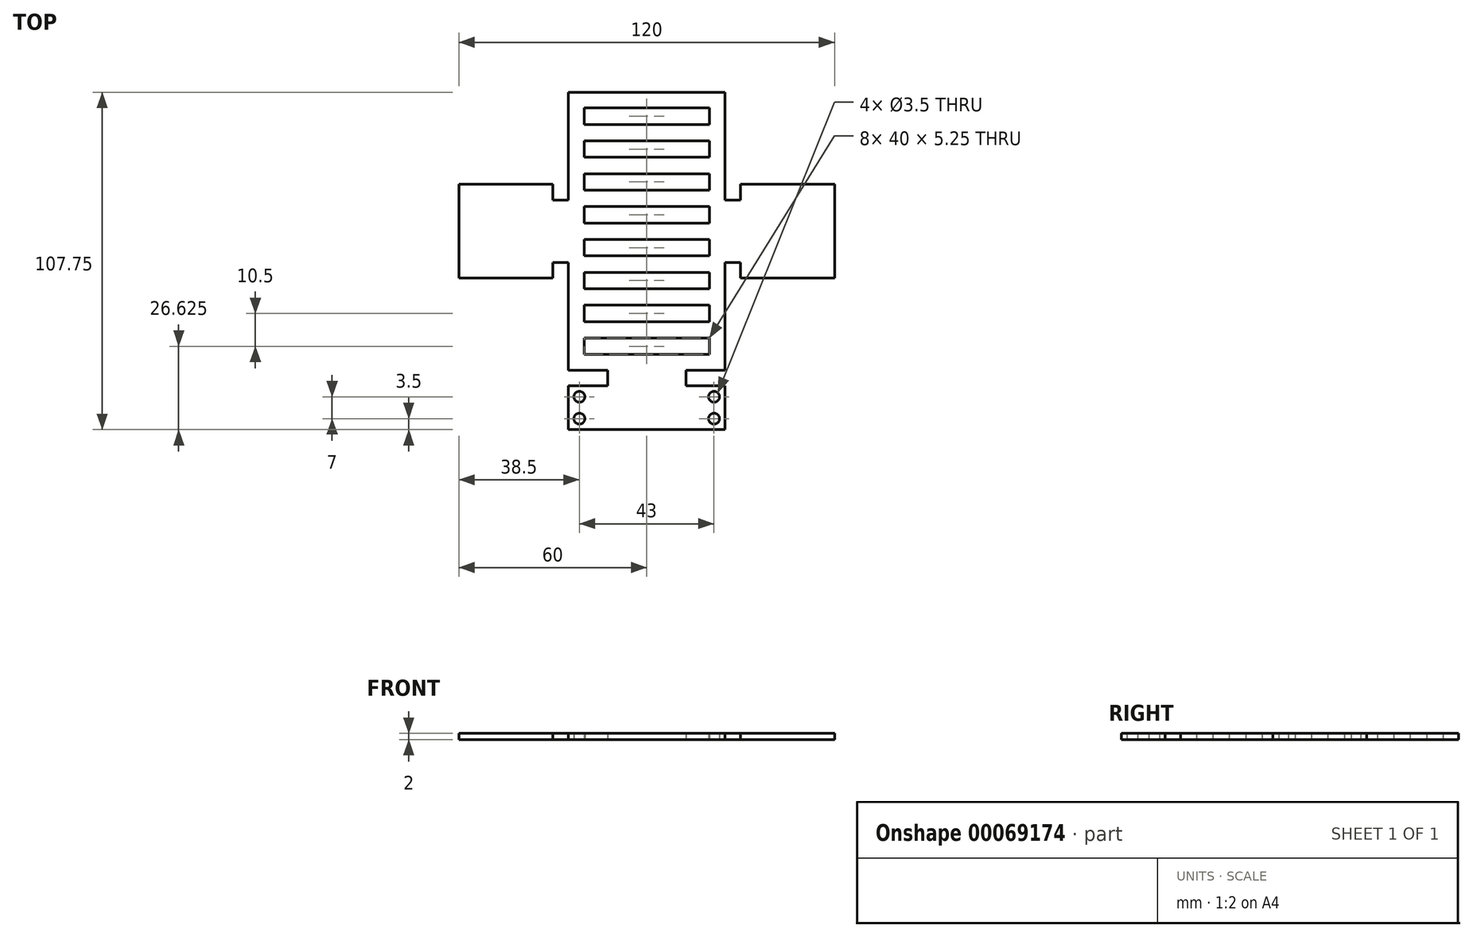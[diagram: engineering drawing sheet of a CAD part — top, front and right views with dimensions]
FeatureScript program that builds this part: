
annotation { "Feature Type Name" : "Feature", "Feature Type Description" : "" }
export const myFeature = defineFeature(function(context is Context, id is Id, definition is map)
    precondition{}
    {
        {
            var Q0;
            Q0=qCreatedBy(makeId("Top.planeOp"),FACE);
            var sketch = newSketch(context, id + "F0", { "sketchPlane" : qUnion([Q0])});
            skLineSegment(sketch, "E0", {"start": v(0, 0) * mm, "end": v(0, 29.37) * mm});
            skLineSegment(sketch, "E1", {"start": v(-5, 29.38) * mm, "end": v(-35, 29.38) * mm});
            skLineSegment(sketch, "E2", {"start": v(-35, 29.38) * mm, "end": v(-35, 59.38) * mm});
            skLineSegment(sketch, "E3", {"start": v(-35, 59.38) * mm, "end": v(-5, 59.38) * mm});
            skLineSegment(sketch, "E4", {"start": v(0, 59.38) * mm, "end": v(0, 88.75) * mm});
            skLineSegment(sketch, "E5", {"start": v(0, 88.75) * mm, "end": v(25, 88.75) * mm});
            skLineSegment(sketch, "E6", {"start": v(0, 0) * mm, "end": v(25, 0) * mm});
            skLineSegment(sketch, "E7", {"start": v(25, 88.75) * mm, "end": v(25, -19) * mm, "construction": true});
            skLineSegment(sketch, "E8", {"start": v(0, -5) * mm, "end": v(0, -19) * mm});
            skLineSegment(sketch, "E9", {"start": v(0, -19) * mm, "end": v(25, -19) * mm});
            skCircle(sketch, "E10.cCircle", {"center": v(-20, 44.37) * mm, "radius": 10 * mm, "construction": true});
            skPoint(sketch, "E10.cCircle.centerSnap0", {"position": v(-35, 44.38) * mm});
            skLineSegment(sketch, "E10.0", {"start": v(-14.23, 54.37) * mm, "end": v(-8.45, 44.37) * mm, "construction": true});
            skLineSegment(sketch, "E10.1", {"start": v(-8.45, 44.37) * mm, "end": v(-14.23, 34.37) * mm, "construction": true});
            skLineSegment(sketch, "E10.2", {"start": v(-14.23, 34.37) * mm, "end": v(-25.77, 34.37) * mm, "construction": true});
            skLineSegment(sketch, "E10.3", {"start": v(-25.77, 34.37) * mm, "end": v(-31.55, 44.37) * mm, "construction": true});
            skLineSegment(sketch, "E10.4", {"start": v(-31.55, 44.37) * mm, "end": v(-25.77, 54.37) * mm, "construction": true});
            skLineSegment(sketch, "E10.5", {"start": v(-25.77, 54.37) * mm, "end": v(-14.23, 54.37) * mm, "construction": true});
            skPoint(sketch, "E10.0.midPoint", {"position": v(-11.34, 49.37) * mm});
            skLineSegment(sketch, "E11", {"start": v(25, 83.75) * mm, "end": v(5, 83.75) * mm});
            skLineSegment(sketch, "E12", {"start": v(5, 83.75) * mm, "end": v(5, 78.5) * mm});
            skLineSegment(sketch, "E13", {"start": v(5, 78.5) * mm, "end": v(25, 78.5) * mm});
            skLineSegment(sketch, "E14.0.1.0", {"start": v(5, 68) * mm, "end": v(25, 68) * mm});
            skLineSegment(sketch, "E14.0.1.1", {"start": v(5, 73.25) * mm, "end": v(5, 68) * mm});
            skLineSegment(sketch, "E14.0.1.2", {"start": v(25, 73.25) * mm, "end": v(5, 73.25) * mm});
            skLineSegment(sketch, "E14.0.2.0", {"start": v(5, 57.5) * mm, "end": v(25, 57.5) * mm});
            skLineSegment(sketch, "E14.0.2.1", {"start": v(5, 62.75) * mm, "end": v(5, 57.5) * mm});
            skLineSegment(sketch, "E14.0.2.2", {"start": v(25, 62.75) * mm, "end": v(5, 62.75) * mm});
            skLineSegment(sketch, "E14.0.3.0", {"start": v(5, 47) * mm, "end": v(25, 47) * mm});
            skLineSegment(sketch, "E14.0.3.1", {"start": v(5, 52.25) * mm, "end": v(5, 47) * mm});
            skLineSegment(sketch, "E14.0.3.2", {"start": v(25, 52.25) * mm, "end": v(5, 52.25) * mm});
            skLineSegment(sketch, "E14.0.4.0", {"start": v(5, 36.5) * mm, "end": v(25, 36.5) * mm});
            skLineSegment(sketch, "E14.0.4.1", {"start": v(5, 41.75) * mm, "end": v(5, 36.5) * mm});
            skLineSegment(sketch, "E14.0.4.2", {"start": v(25, 41.75) * mm, "end": v(5, 41.75) * mm});
            skLineSegment(sketch, "E14.0.5.0", {"start": v(5, 26) * mm, "end": v(25, 26) * mm});
            skLineSegment(sketch, "E14.0.5.1", {"start": v(5, 31.25) * mm, "end": v(5, 26) * mm});
            skLineSegment(sketch, "E14.0.5.2", {"start": v(25, 31.25) * mm, "end": v(5, 31.25) * mm});
            skLineSegment(sketch, "E14.0.6.0", {"start": v(5, 15.5) * mm, "end": v(25, 15.5) * mm});
            skLineSegment(sketch, "E14.0.6.1", {"start": v(5, 20.75) * mm, "end": v(5, 15.5) * mm});
            skLineSegment(sketch, "E14.0.6.2", {"start": v(25, 20.75) * mm, "end": v(5, 20.75) * mm});
            skLineSegment(sketch, "E14.0.7.0", {"start": v(5, 5) * mm, "end": v(25, 5) * mm});
            skLineSegment(sketch, "E14.0.7.1", {"start": v(5, 10.25) * mm, "end": v(5, 5) * mm});
            skLineSegment(sketch, "E14.0.7.2", {"start": v(25, 10.25) * mm, "end": v(5, 10.25) * mm});
            skLineSegment(sketch, "E14.direction1", {"start": v(5, 78.5) * mm, "end": v(25, 78.5) * mm, "construction": true});
            skLineSegment(sketch, "E14.direction2", {"start": v(5, 78.5) * mm, "end": v(5, 68) * mm, "construction": true});
            skCircle(sketch, "E15", {"center": v(3.5, -15.5) * mm, "radius": 1.75 * mm});
            skLineSegment(sketch, "E16", {"start": v(-5, 59.38) * mm, "end": v(-5, 54.38) * mm});
            skLineSegment(sketch, "E17", {"start": v(-5, 54.38) * mm, "end": v(0, 54.38) * mm});
            skLineSegment(sketch, "E18", {"start": v(0, 54.38) * mm, "end": v(0, 59.38) * mm});
            skLineSegment(sketch, "E19", {"start": v(-35, 44.38) * mm, "end": v(25, 44.38) * mm, "construction": true});
            skLineSegment(sketch, "E20.MirrorCS", {"start": v(-5, 29.38) * mm, "end": v(-5, 34.38) * mm});
            skLineSegment(sketch, "E21.MirrorCS", {"start": v(-5, 34.38) * mm, "end": v(0, 34.38) * mm});
            skLineSegment(sketch, "E22.MirrorCS", {"start": v(0, 34.38) * mm, "end": v(0, 29.37) * mm});
            skPoint(sketch, "E23", {"position": v(-20, 59.37) * mm});
            skLineSegment(sketch, "E24", {"start": v(0, -5) * mm, "end": v(12.5, -5) * mm});
            skLineSegment(sketch, "E25", {"start": v(12.5, -5) * mm, "end": v(12.5, 0) * mm});
            skLineSegment(sketch, "E26.MirrorCS", {"start": v(45, 78.5) * mm, "end": v(45, 68) * mm, "construction": true});
            skLineSegment(sketch, "E27.MirrorCS", {"start": v(45, 73.25) * mm, "end": v(45, 68) * mm});
            skCircle(sketch, "E28.MirrorC", {"center": v(46.5, -15.5) * mm, "radius": 1.75 * mm});
            skLineSegment(sketch, "E29.MirrorCS", {"start": v(55, 54.38) * mm, "end": v(50, 54.37) * mm});
            skLineSegment(sketch, "E30.MirrorCS", {"start": v(45, 52.25) * mm, "end": v(45, 47) * mm});
            skLineSegment(sketch, "E31.MirrorCS", {"start": v(45, 83.75) * mm, "end": v(45, 78.5) * mm});
            skLineSegment(sketch, "E32.MirrorCS", {"start": v(45, 31.25) * mm, "end": v(45, 26) * mm});
            skLineSegment(sketch, "E33.MirrorCS", {"start": v(50, 54.37) * mm, "end": v(50, 59.38) * mm});
            skLineSegment(sketch, "E34.MirrorCS", {"start": v(45, 62.75) * mm, "end": v(45, 57.5) * mm});
            skLineSegment(sketch, "E35.MirrorCS", {"start": v(55, 29.38) * mm, "end": v(55, 34.37) * mm});
            skLineSegment(sketch, "E36.MirrorCS", {"start": v(45, 20.75) * mm, "end": v(45, 15.5) * mm});
            skLineSegment(sketch, "E37.MirrorCS", {"start": v(45, 41.75) * mm, "end": v(45, 36.5) * mm});
            skLineSegment(sketch, "E38.MirrorCS", {"start": v(55, 34.38) * mm, "end": v(50, 34.38) * mm});
            skLineSegment(sketch, "E39.MirrorCS", {"start": v(50, 34.38) * mm, "end": v(50, 29.38) * mm});
            skLineSegment(sketch, "E40.MirrorCS", {"start": v(37.5, -5) * mm, "end": v(37.5, 0) * mm});
            skLineSegment(sketch, "E41.MirrorCS", {"start": v(45, 10.25) * mm, "end": v(45, 5) * mm});
            skLineSegment(sketch, "E42.MirrorCS", {"start": v(55, 59.37) * mm, "end": v(55, 54.38) * mm});
            skLineSegment(sketch, "E43.MirrorCS", {"start": v(45, 78.5) * mm, "end": v(25, 78.5) * mm, "construction": true});
            skLineSegment(sketch, "E44.MirrorCS", {"start": v(64.23, 34.37) * mm, "end": v(75.77, 34.37) * mm, "construction": true});
            skLineSegment(sketch, "E45.MirrorCS", {"start": v(64.23, 54.38) * mm, "end": v(58.45, 44.38) * mm, "construction": true});
            skLineSegment(sketch, "E46.MirrorCS", {"start": v(25, 41.75) * mm, "end": v(45, 41.75) * mm});
            skLineSegment(sketch, "E47.MirrorCS", {"start": v(50, -5) * mm, "end": v(37.5, -5) * mm});
            skLineSegment(sketch, "E48.MirrorCS", {"start": v(45, 5) * mm, "end": v(25, 5) * mm});
            skLineSegment(sketch, "E49.MirrorCS", {"start": v(45, 26) * mm, "end": v(25, 26) * mm});
            skLineSegment(sketch, "E50.MirrorCS", {"start": v(50, 0) * mm, "end": v(25, 0) * mm});
            skPoint(sketch, "E51.MirrorP", {"position": v(70, 59.38) * mm});
            skLineSegment(sketch, "E52.MirrorCS", {"start": v(45, 78.5) * mm, "end": v(25, 78.5) * mm});
            skLineSegment(sketch, "E53.MirrorCS", {"start": v(50, 59.38) * mm, "end": v(50, 88.75) * mm});
            skLineSegment(sketch, "E54.MirrorCS", {"start": v(50, 88.75) * mm, "end": v(25, 88.75) * mm});
            skLineSegment(sketch, "E55.MirrorCS", {"start": v(85, 59.38) * mm, "end": v(55, 59.38) * mm});
            skLineSegment(sketch, "E56.MirrorCS", {"start": v(45, 47) * mm, "end": v(25, 47) * mm});
            skPoint(sketch, "E57.MirrorP", {"position": v(61.34, 49.38) * mm});
            skPoint(sketch, "E58.MirrorP", {"position": v(85, 44.38) * mm});
            skLineSegment(sketch, "E59.MirrorCS", {"start": v(55, 29.38) * mm, "end": v(85, 29.38) * mm});
            skLineSegment(sketch, "E60.MirrorCS", {"start": v(25, 52.25) * mm, "end": v(45, 52.25) * mm});
            skLineSegment(sketch, "E61.MirrorCS", {"start": v(25, 10.25) * mm, "end": v(45, 10.25) * mm});
            skLineSegment(sketch, "E62.MirrorCS", {"start": v(45, 36.5) * mm, "end": v(25, 36.5) * mm});
            skLineSegment(sketch, "E63.MirrorCS", {"start": v(75.77, 54.37) * mm, "end": v(64.23, 54.37) * mm, "construction": true});
            skCircle(sketch, "E64.MirrorC", {"center": v(70, 44.38) * mm, "radius": 10 * mm, "construction": true});
            skLineSegment(sketch, "E65.MirrorCS", {"start": v(81.55, 44.37) * mm, "end": v(75.77, 54.38) * mm, "construction": true});
            skLineSegment(sketch, "E66.MirrorCS", {"start": v(45, 68) * mm, "end": v(25, 68) * mm});
            skLineSegment(sketch, "E67.MirrorCS", {"start": v(85, 29.38) * mm, "end": v(85, 59.37) * mm});
            skLineSegment(sketch, "E68.MirrorCS", {"start": v(75.77, 34.37) * mm, "end": v(81.55, 44.37) * mm, "construction": true});
            skLineSegment(sketch, "E69.MirrorCS", {"start": v(45, 57.5) * mm, "end": v(25, 57.5) * mm});
            skLineSegment(sketch, "E70.MirrorCS", {"start": v(25, 73.25) * mm, "end": v(45, 73.25) * mm});
            skLineSegment(sketch, "E71.MirrorCS", {"start": v(25, 62.75) * mm, "end": v(45, 62.75) * mm});
            skLineSegment(sketch, "E72.MirrorCS", {"start": v(85, 44.38) * mm, "end": v(25, 44.38) * mm, "construction": true});
            skLineSegment(sketch, "E73.MirrorCS", {"start": v(58.45, 44.38) * mm, "end": v(64.23, 34.38) * mm, "construction": true});
            skLineSegment(sketch, "E74.MirrorCS", {"start": v(25, 20.75) * mm, "end": v(45, 20.75) * mm});
            skLineSegment(sketch, "E75.MirrorCS", {"start": v(25, 83.75) * mm, "end": v(45, 83.75) * mm});
            skLineSegment(sketch, "E76.MirrorCS", {"start": v(50, 0) * mm, "end": v(50, 29.38) * mm});
            skLineSegment(sketch, "E77.MirrorCS", {"start": v(50, -19) * mm, "end": v(25, -19) * mm});
            skLineSegment(sketch, "E78.MirrorCS", {"start": v(50, -5) * mm, "end": v(50, -19) * mm});
            skLineSegment(sketch, "E79.MirrorCS", {"start": v(45, 15.5) * mm, "end": v(25, 15.5) * mm});
            skLineSegment(sketch, "E80.MirrorCS", {"start": v(25, 31.25) * mm, "end": v(45, 31.25) * mm});
            skLineSegment(sketch, "E81", {"start": v(0, -12) * mm, "end": v(25, -12) * mm, "construction": true});
            skCircle(sketch, "E82.MirrorC", {"center": v(3.5, -8.5) * mm, "radius": 1.75 * mm});
            skCircle(sketch, "E83.MirrorC", {"center": v(46.5, -8.5) * mm, "radius": 1.75 * mm});
            skSolve(sketch);
        }
        {
            var Q0;
            Q0=makeQuery(id+"F0.imprint","IMPRINT",FACE,{"disambiguationData":[TD([[makeQuery(id+"F0.imprint","IMPRINT",EDGE,{"derivedFrom":sQuery(id+"F0.wireOp",EDGE,"E6")}),-1.0]])]});
            var Q1;
            Q1=makeQuery(id+"F0.imprint","IMPRINT",FACE,{"disambiguationData":[TD([[makeQuery(id+"F0.imprint","IMPRINT",EDGE,{"derivedFrom":sQuery(id+"F0.wireOp",EDGE,"E0")}),-1.0]])]});
            extrude(context, id + "F1", {"entities" : qUnion([Q0, Q1]), "depth" : 2 * mm});
        }
    });
